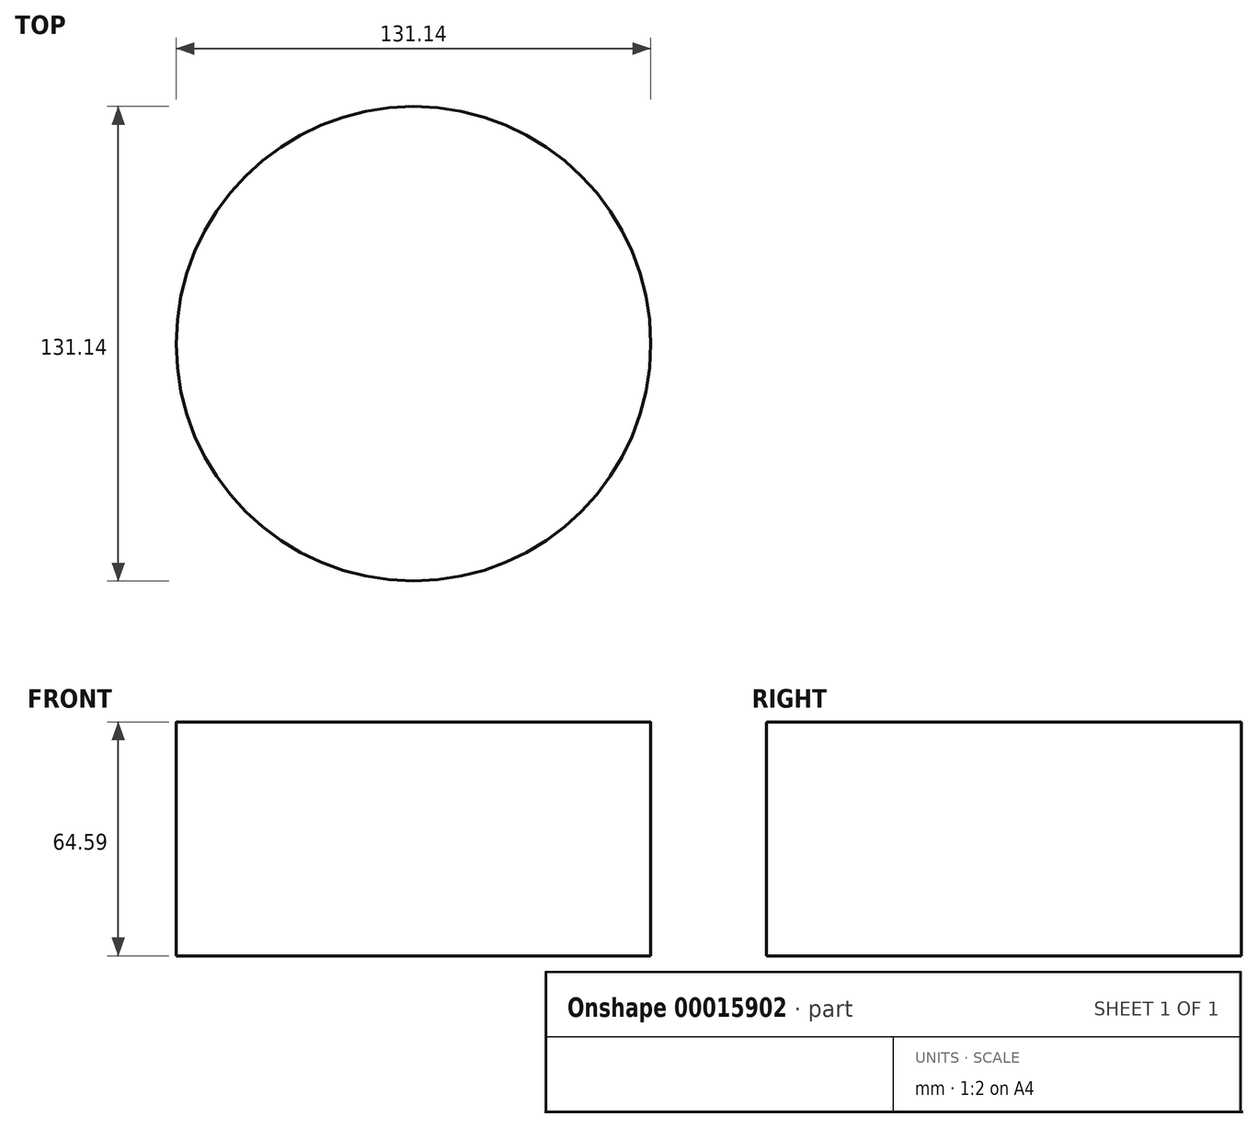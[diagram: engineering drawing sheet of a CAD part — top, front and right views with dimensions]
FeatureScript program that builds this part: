
annotation { "Feature Type Name" : "Feature", "Feature Type Description" : "" }
export const myFeature = defineFeature(function(context is Context, id is Id, definition is map)
    precondition{}
    {
        {
            var Q0;
            Q0=qCreatedBy(makeId("Top.planeOp"),FACE);
            var sketch = newSketch(context, id + "F0", { "sketchPlane" : qUnion([Q0])});
            skArc(sketch, "E0", {"start": v(-65.57, 0.03) * mm, "mid": v(-0.02, -65.57) * mm, "end": v(65.57, 0) * mm});
            skArc(sketch, "E1", {"start": v(65.57, 0) * mm, "mid": v(0.02, 65.57) * mm, "end": v(-65.57, 0.03) * mm});
            skSolve(sketch);
        }
        {
            var Q0;
            Q0=qCreatedBy(makeId("Front.planeOp"),FACE);
            var sketch = newSketch(context, id + "F1", { "sketchPlane" : qUnion([Q0])});
            skLineSegment(sketch, "E2", {"start": v(0, 0) * mm, "end": v(0, 64.59) * mm});
            skSolve(sketch);
        }
        {
            var Q0;
            Q0=makeQuery(id+"F0.imprint","IMPRINT",FACE,{"disambiguationData":[TD([[makeQuery(id+"F0.imprint","IMPRINT",EDGE,{"derivedFrom":sQuery(id+"F0.wireOp",EDGE,"E0")}),1.0]])]});
            var Q1;
            Q1=sQuery(id+"F1.wireOp",EDGE,"E2");
            sweep(context, id + "F2", {"profiles" : qUnion([Q0]), "path" : qUnion([Q1])});
        }
        {
            var Q0;
            Q0=makeQuery(id+"F2.opSweep","CAP_EDGE",EDGE,{"disambiguationData":[OSD([sQuery(id+"F0.wireOp",EDGE,"E0"),sQuery(id+"F0.wireOp",EDGE,"E1"),sQuery(id+"F1.wireOp",VERTEX,"E2.end")])],"isStart":false});
            fillet(context, id + "F3", {"entities" : qUnion([Q0]), "radius" : 5.16 / 50.8 * mm, "tangentPropagation" : true, "allowEdgeOverflow" : false});
        }
        {
            var Q0;
            Q0=qCreatedBy(makeId("Top.planeOp"),FACE);
            var sketch = newSketch(context, id + "F4", { "sketchPlane" : qUnion([Q0])});
            skArc(sketch, "E3", {"start": v(62.62, 18.54) * mm, "mid": v(-0.43, 99.81) * mm, "end": v(-63.48, 18.54) * mm});
            skSolve(sketch);
        }
    });
